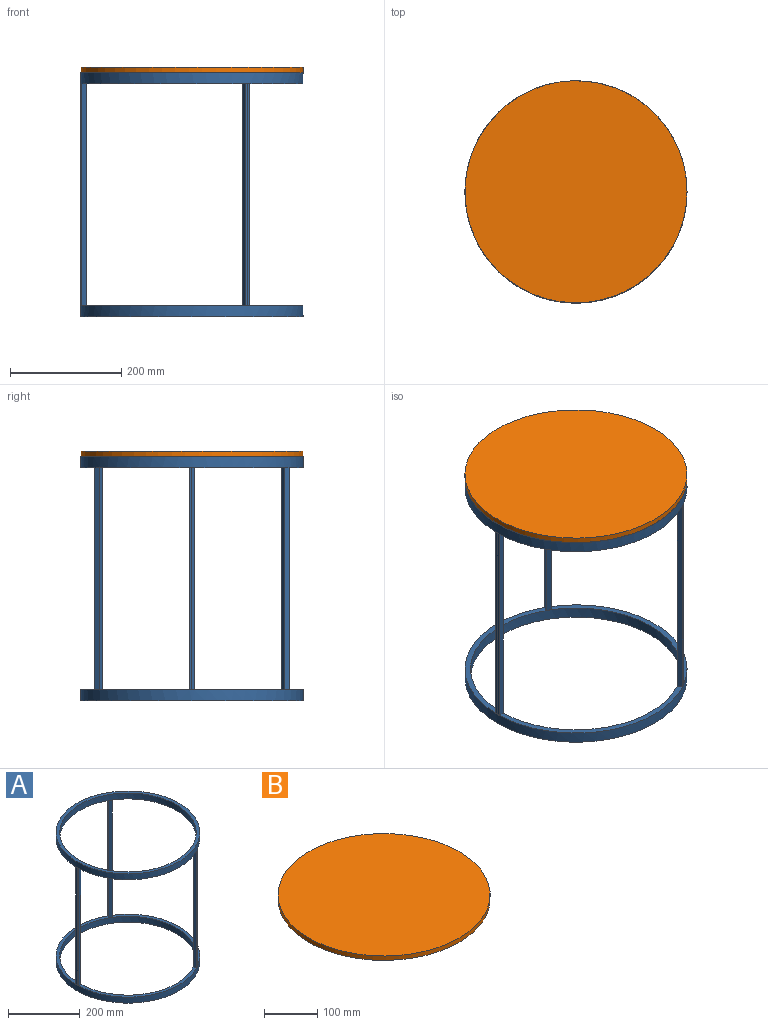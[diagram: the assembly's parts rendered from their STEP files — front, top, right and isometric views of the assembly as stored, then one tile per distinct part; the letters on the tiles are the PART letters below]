
ASSEMBLY  parts=2 mates=1
PART A: 42 faces, bbox 400x400x440 mm
  f0: plane 295.58x195.13mm, normal (0,0,1), area 3984.1mm2, adj f8,f9,f13,f14,f25,f29
  f1: plane 341.3x100.81mm, normal (0,0,1), area 3984.1mm2, adj f8,f9,f19,f23,f25,f26
  f2: plane 4.3x2.55mm, normal (0,0,1), area 0.1mm2, adj f9,f27
  f3: plane 4.36x2.45mm, normal (0,0,1), area 0.1mm2, adj f9,f28
  f4: plane 295.58x195.13mm, normal (0,0,1), area 3984.1mm2, adj f8,f9,f13,f17,f19,f20
  f5: plane 4.36x2.45mm, normal (0,0,1), area 0.1mm2, adj f9,f21
  f6: plane 4.3x2.55mm, normal (0,0,1), area 0.1mm2, adj f9,f22
  f7: plane 5x0.06mm, normal (0,0,1), area 0.1mm2, adj f9,f15
  f8: cylinder r=190mm len=380mm, axis (0,0,-1), area 23876.1mm2, adj f0,f1,f4,f11,f12,f18,f24
  f9: cylinder r=200mm len=400mm, axis (0,0,-1), area 25132.7mm2, adj f0,f1,f2,f3,f4,f5,f6,f7
  f10: plane 5x0.06mm, normal (0,0,1), area 0.1mm2, adj f9,f16
  f11: plane 400x400mm, normal (0,0,-1), area 12252.2mm2, adj f8,f9
  f12: plane 9.75x0.06mm, normal (0,0,-1), area 0.4mm2, adj f8,f13
  f13: plane 400x10mm, normal (1,0,0), area 4000mm2, adj f0,f4,f12,f14,f17,f30,f31
  f14: plane 400x10mm, normal (0,1,0), area 4000mm2, adj f0,f13,f15,f30
  f15: plane 400x5mm, normal (-1,0.01,0), area 2000.2mm2, adj f7,f14,f16,f32
  f16: plane 400x5mm, normal (-1,-0.01,0), area 2000.2mm2, adj f10,f15,f17,f35
  f17: plane 400x10mm, normal (0,-1,0), area 4000mm2, adj f4,f13,f16,f31
  f18: plane 8.44x4.87mm, normal (0,0,-1), area 0.4mm2, adj f8,f19
  f19: plane 400x8.66mm, normal (-0.5,0.87,0), area 4000mm2, adj f1,f4,f18,f20,f23,f31,f33
  f20: plane 400x8.66mm, normal (-0.87,-0.5,0), area 4000mm2, adj f4,f19,f21,f31
  f21: plane 400x4.36mm, normal (0.49,-0.87,0), area 2000.2mm2, adj f5,f20,f22,f34
  f22: plane 400x4.3mm, normal (0.51,-0.86,0), area 2000.2mm2, adj f6,f21,f23,f37
  f23: plane 400x8.66mm, normal (0.87,0.5,0), area 4000mm2, adj f1,f19,f22,f33
  f24: plane 8.44x4.87mm, normal (0,0,-1), area 0.4mm2, adj f8,f25
  f25: plane 400x8.66mm, normal (-0.5,-0.87,0), area 4000mm2, adj f0,f1,f24,f26,f29,f30,f33
  f26: plane 400x8.66mm, normal (0.87,-0.5,0), area 4000mm2, adj f1,f25,f27,f33
  f27: plane 400x4.3mm, normal (0.51,0.86,0), area 2000.2mm2, adj f2,f26,f28,f36
  f28: plane 400x4.36mm, normal (0.49,0.87,0), area 2000.2mm2, adj f3,f27,f29,f41
  f29: plane 400x8.66mm, normal (-0.87,0.5,0), area 4000mm2, adj f0,f25,f28,f30
  f30: plane 295.58x200mm, normal (0,0,-1), area 4008.5mm2, adj f13,f14,f25,f29,f38,f39
  f31: plane 295.58x200mm, normal (0,0,-1), area 4008.5mm2, adj f13,f17,f19,f20,f38,f39
  f32: plane 5x0.06mm, normal (0,0,-1), area 0.1mm2, adj f15,f38
  f33: plane 341.3x105.03mm, normal (0,0,-1), area 4008.5mm2, adj f19,f23,f25,f26,f38,f39
  f34: plane 4.36x2.45mm, normal (0,0,-1), area 0.1mm2, adj f21,f38
  f35: plane 5x0.06mm, normal (0,0,-1), area 0.1mm2, adj f16,f38
  f36: plane 4.3x2.55mm, normal (0,0,-1), area 0.1mm2, adj f27,f38
  f37: plane 4.3x2.55mm, normal (0,0,-1), area 0.1mm2, adj f22,f38
  f38: cylinder r=200mm len=400mm, axis (0,0,-1), area 25132.7mm2, adj f30,f31,f32,f33,f34,f35,f36,f37
  f39: cylinder r=189.94mm len=379.88mm, axis (0,0,-1), area 23868.2mm2, adj f30,f31,f33,f40
  f40: plane 400x400mm, normal (0,0,1), area 12326.8mm2, adj f38,f39
  f41: plane 4.36x2.45mm, normal (0,0,-1), area 0.1mm2, adj f28,f38
PART B: 3 faces, bbox 400x400x10 mm
  f0: cylinder r=200mm len=400mm, axis (0,0,-1), area 12566.4mm2, adj f1,f2
  f1: plane 400x400mm, normal (0,0,1), area 125663.7mm2, adj f0
  f2: plane 400x400mm, normal (0,0,-1), area 125663.7mm2, adj f0
PLACE A t=(375.69,359.77,-230.71)mm
PLACE B t=(375.69,359.77,209.29)mm
MATE fastened A.f39 <-> B.f0  axis (0,0,1) through (375.69,359.77,209.29)mm
